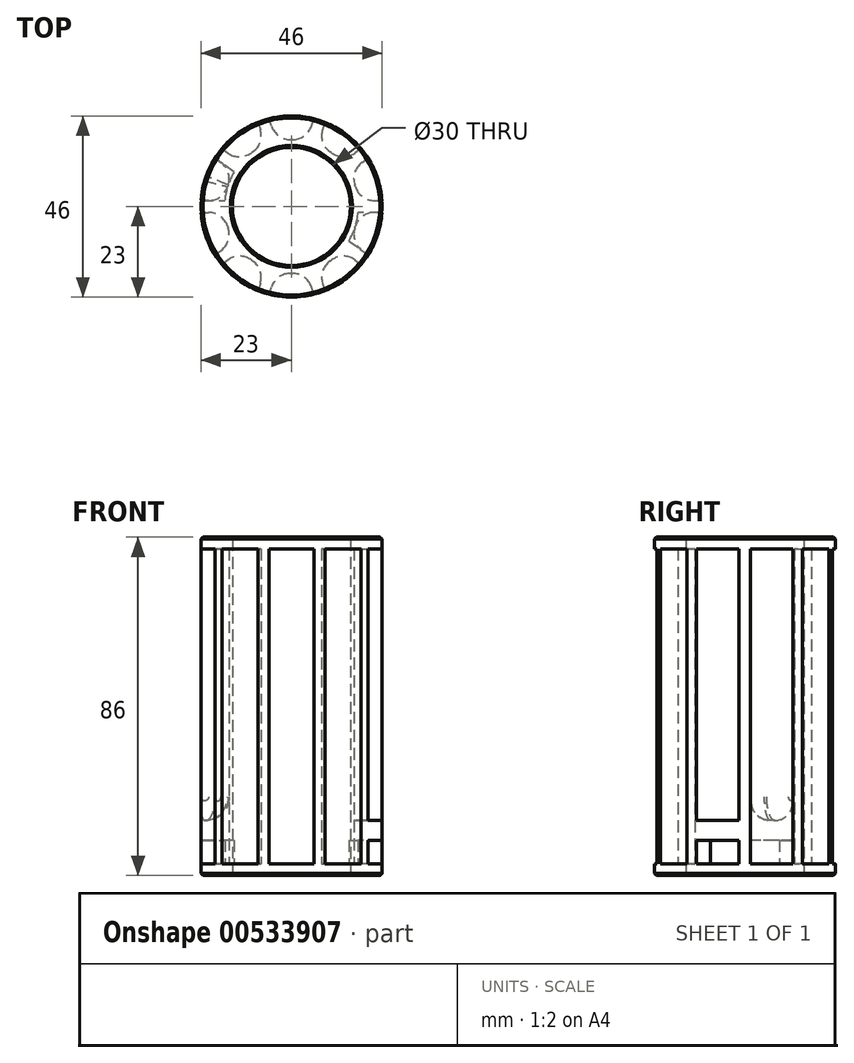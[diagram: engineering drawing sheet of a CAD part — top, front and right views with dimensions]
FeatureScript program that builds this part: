
annotation { "Feature Type Name" : "Feature", "Feature Type Description" : "" }
export const myFeature = defineFeature(function(context is Context, id is Id, definition is map)
    precondition{}
    {
        {
            var Q0;
            Q0=qCreatedBy(makeId("Top.planeOp"),FACE);
            var sketch = newSketch(context, id + "F0", { "sketchPlane" : qUnion([Q0])});
            skCircle(sketch, "E0", {"center": v(0, 0) * mm, "radius": 15 * mm});
            skArc(sketch, "E1", {"start": v(-14.58, 8.74) * mm, "mid": v(-16.17, 5.25) * mm, "end": v(-16.93, 1.5) * mm});
            skLineSegment(sketch, "E2.bottom", {"start": v(22.95, -1.5) * mm, "end": v(16.93, -1.5) * mm});
            skLineSegment(sketch, "E2.top", {"start": v(22.95, 1.5) * mm, "end": v(16.93, 1.5) * mm});
            skLineSegment(sketch, "E3.trimOffspring", {"start": v(-16.93, 1.5) * mm, "end": v(-22.95, 1.5) * mm});
            skLineSegment(sketch, "E4.trimOffspring", {"start": v(-16.93, -1.5) * mm, "end": v(-22.95, -1.5) * mm});
            skPoint(sketch, "E5.orphan", {"position": v(-19.5, -1.5) * mm});
            skPoint(sketch, "E6.orphan", {"position": v(-19.5, 1.5) * mm});
            skPoint(sketch, "E7.orphan", {"position": v(19.5, 1.5) * mm});
            skPoint(sketch, "E2.left.start.orphan", {"position": v(19.5, -1.5) * mm});
            skLineSegment(sketch, "E8.1.0", {"start": v(-6.66, -15.64) * mm, "end": v(-8.52, -21.36) * mm});
            skLineSegment(sketch, "E8.1.1", {"start": v(-3.8, -16.57) * mm, "end": v(-5.67, -22.3) * mm});
            skLineSegment(sketch, "E8.1.2", {"start": v(8.52, 21.36) * mm, "end": v(6.66, 15.64) * mm});
            skLineSegment(sketch, "E8.1.3", {"start": v(5.67, 22.3) * mm, "end": v(3.8, 16.57) * mm});
            skLineSegment(sketch, "E8.2.0", {"start": v(12.82, -11.17) * mm, "end": v(17.69, -14.7) * mm});
            skLineSegment(sketch, "E8.2.1", {"start": v(14.58, -8.74) * mm, "end": v(19.45, -12.28) * mm});
            skLineSegment(sketch, "E8.2.2", {"start": v(-17.69, 14.7) * mm, "end": v(-12.82, 11.17) * mm});
            skLineSegment(sketch, "E8.2.3", {"start": v(-19.45, 12.28) * mm, "end": v(-14.58, 8.74) * mm});
            skLineSegment(sketch, "E8.3.0", {"start": v(14.58, 8.74) * mm, "end": v(19.45, 12.28) * mm});
            skLineSegment(sketch, "E8.3.1", {"start": v(12.82, 11.17) * mm, "end": v(17.69, 14.7) * mm});
            skLineSegment(sketch, "E8.3.2", {"start": v(-19.45, -12.28) * mm, "end": v(-14.58, -8.74) * mm});
            skLineSegment(sketch, "E8.3.3", {"start": v(-17.69, -14.7) * mm, "end": v(-12.82, -11.17) * mm});
            skLineSegment(sketch, "E8.4.0", {"start": v(-3.8, 16.57) * mm, "end": v(-5.67, 22.3) * mm});
            skLineSegment(sketch, "E8.4.1", {"start": v(-6.66, 15.64) * mm, "end": v(-8.52, 21.36) * mm});
            skLineSegment(sketch, "E8.4.2", {"start": v(5.67, -22.3) * mm, "end": v(3.8, -16.57) * mm});
            skLineSegment(sketch, "E8.4.3", {"start": v(8.52, -21.36) * mm, "end": v(6.66, -15.64) * mm});
            skPoint(sketch, "E9.orphan", {"position": v(-16.93, 1.5) * mm});
            skPoint(sketch, "E10.orphan", {"position": v(-16.93, -1.5) * mm});
            skPoint(sketch, "E11.orphan", {"position": v(-14.58, -8.74) * mm});
            skPoint(sketch, "E12.orphan", {"position": v(-12.82, -11.17) * mm});
            skPoint(sketch, "E13.orphan", {"position": v(-14.58, 8.74) * mm});
            skPoint(sketch, "E14.orphan", {"position": v(-12.82, 11.17) * mm});
            skPoint(sketch, "E15.orphan", {"position": v(-6.66, 15.64) * mm});
            skPoint(sketch, "E16.orphan", {"position": v(-3.8, 16.57) * mm});
            skPoint(sketch, "E17.orphan", {"position": v(3.8, 16.57) * mm});
            skPoint(sketch, "E18.orphan", {"position": v(6.66, 15.64) * mm});
            skPoint(sketch, "E19.orphan", {"position": v(12.82, 11.17) * mm});
            skPoint(sketch, "E20.orphan", {"position": v(14.58, 8.74) * mm});
            skPoint(sketch, "E21.orphan", {"position": v(16.93, 1.5) * mm});
            skPoint(sketch, "E22.orphan", {"position": v(16.93, -1.5) * mm});
            skPoint(sketch, "E23.orphan", {"position": v(14.58, -8.74) * mm});
            skPoint(sketch, "E24.orphan", {"position": v(12.82, -11.17) * mm});
            skPoint(sketch, "E25.orphan", {"position": v(6.66, -15.64) * mm});
            skPoint(sketch, "E26.orphan", {"position": v(3.8, -16.57) * mm});
            skPoint(sketch, "E27.orphan", {"position": v(-3.8, -16.57) * mm});
            skPoint(sketch, "E28.orphan", {"position": v(-6.66, -15.64) * mm});
            skCircle(sketch, "E29.0", {"center": v(0, 0) * mm, "radius": 23 * mm});
            skPoint(sketch, "E30.orphan", {"position": v(-12.96, 7.56) * mm});
            skPoint(sketch, "E31.orphan", {"position": v(-11.2, 9.99) * mm});
            skArc(sketch, "E32.trimOffspring", {"start": v(-6.66, 15.64) * mm, "mid": v(-10, 13.75) * mm, "end": v(-12.82, 11.17) * mm});
            skPoint(sketch, "E33.orphan", {"position": v(-3.19, 14.66) * mm});
            skPoint(sketch, "E34.orphan", {"position": v(-6.04, 13.73) * mm});
            skPoint(sketch, "E35.orphan", {"position": v(3.19, 14.66) * mm});
            skArc(sketch, "E36.trimOffspring", {"start": v(3.8, 16.57) * mm, "mid": v(0, 17) * mm, "end": v(-3.8, 16.57) * mm});
            skPoint(sketch, "E37.orphan", {"position": v(6.04, 13.73) * mm});
            skPoint(sketch, "E38.orphan", {"position": v(11.2, 9.99) * mm});
            skArc(sketch, "E39.trimOffspring", {"start": v(12.82, 11.17) * mm, "mid": v(10, 13.75) * mm, "end": v(6.66, 15.64) * mm});
            skPoint(sketch, "E40.orphan", {"position": v(12.96, 7.56) * mm});
            skPoint(sketch, "E41.orphan", {"position": v(14.92, 1.5) * mm});
            skArc(sketch, "E42.trimOffspring", {"start": v(16.93, 1.5) * mm, "mid": v(16.17, 5.25) * mm, "end": v(14.58, 8.74) * mm});
            skPoint(sketch, "E43.orphan", {"position": v(14.92, -1.5) * mm});
            skPoint(sketch, "E44.orphan", {"position": v(12.96, -7.56) * mm});
            skArc(sketch, "E45.trimOffspring", {"start": v(14.58, -8.74) * mm, "mid": v(16.17, -5.25) * mm, "end": v(16.93, -1.5) * mm});
            skPoint(sketch, "E46.orphan", {"position": v(11.2, -9.99) * mm});
            skPoint(sketch, "E47.orphan", {"position": v(6.04, -13.73) * mm});
            skArc(sketch, "E48.trimOffspring", {"start": v(6.66, -15.64) * mm, "mid": v(10, -13.75) * mm, "end": v(12.82, -11.17) * mm});
            skPoint(sketch, "E49.orphan", {"position": v(3.19, -14.66) * mm});
            skPoint(sketch, "E50.orphan", {"position": v(-3.19, -14.66) * mm});
            skArc(sketch, "E51.trimOffspring", {"start": v(-3.8, -16.57) * mm, "mid": v(0, -17) * mm, "end": v(3.8, -16.57) * mm});
            skPoint(sketch, "E52.orphan", {"position": v(-6.04, -13.73) * mm});
            skPoint(sketch, "E53.orphan", {"position": v(-11.2, -9.99) * mm});
            skArc(sketch, "E54.trimOffspring", {"start": v(-12.82, -11.17) * mm, "mid": v(-10, -13.75) * mm, "end": v(-6.66, -15.64) * mm});
            skPoint(sketch, "E55.orphan", {"position": v(-12.96, -7.56) * mm});
            skPoint(sketch, "E56.orphan", {"position": v(-14.92, -1.5) * mm});
            skArc(sketch, "E57.trimOffspring", {"start": v(-16.93, -1.5) * mm, "mid": v(-16.17, -5.25) * mm, "end": v(-14.58, -8.74) * mm});
            skPoint(sketch, "E58.orphan", {"position": v(-14.92, 1.5) * mm});
            skSolve(sketch);
        }
        {
            var Q0;
            Q0=makeQuery(id+"F0.imprint","IMPRINT",FACE,{"disambiguationData":[TD([[makeQuery(id+"F0.imprint","IMPRINT",EDGE,{"derivedFrom":sQuery(id+"F0.wireOp",EDGE,"E0")}),-1.0]])]});
            extrude(context, id + "F1", {"entities" : qUnion([Q0]), "depth" : 86 * mm, "offsetDistance" : 25 * mm});
        }
        {
            var Q0;
            Q0=makeQuery(id+"F1.opExtrude","CAP_FACE",FACE,{"disambiguationData":[OSD([sQuery(id+"F0.wireOp",EDGE,"E0"),sQuery(id+"F0.wireOp",EDGE,"E1"),sQuery(id+"F0.wireOp",EDGE,"E2.bottom"),sQuery(id+"F0.wireOp",EDGE,"E2.top"),sQuery(id+"F0.wireOp",EDGE,"E3.trimOffspring"),sQuery(id+"F0.wireOp",EDGE,"E4.trimOffspring"),sQuery(id+"F0.wireOp",EDGE,"E8.1.0"),sQuery(id+"F0.wireOp",EDGE,"E8.1.1"),sQuery(id+"F0.wireOp",EDGE,"E8.1.2"),sQuery(id+"F0.wireOp",EDGE,"E8.1.3"),sQuery(id+"F0.wireOp",EDGE,"E8.2.0"),sQuery(id+"F0.wireOp",EDGE,"E8.2.1"),sQuery(id+"F0.wireOp",EDGE,"E8.2.2"),sQuery(id+"F0.wireOp",EDGE,"E8.2.3"),sQuery(id+"F0.wireOp",EDGE,"E8.3.0"),sQuery(id+"F0.wireOp",EDGE,"E8.3.1"),sQuery(id+"F0.wireOp",EDGE,"E8.3.2"),sQuery(id+"F0.wireOp",EDGE,"E8.3.3"),sQuery(id+"F0.wireOp",EDGE,"E8.4.0"),sQuery(id+"F0.wireOp",EDGE,"E8.4.1"),sQuery(id+"F0.wireOp",EDGE,"E8.4.2"),sQuery(id+"F0.wireOp",EDGE,"E8.4.3"),sQuery(id+"F0.wireOp",EDGE,"E29.0"),sQuery(id+"F0.wireOp",EDGE,"E32.trimOffspring"),sQuery(id+"F0.wireOp",EDGE,"E36.trimOffspring"),sQuery(id+"F0.wireOp",EDGE,"E39.trimOffspring"),sQuery(id+"F0.wireOp",EDGE,"E42.trimOffspring"),sQuery(id+"F0.wireOp",EDGE,"E45.trimOffspring"),sQuery(id+"F0.wireOp",EDGE,"E48.trimOffspring"),sQuery(id+"F0.wireOp",EDGE,"E51.trimOffspring"),sQuery(id+"F0.wireOp",EDGE,"E54.trimOffspring"),sQuery(id+"F0.wireOp",EDGE,"E57.trimOffspring")])],"isStart":true});
            var sketch = newSketch(context, id + "F2", { "sketchPlane" : qUnion([Q0])});
            skCircle(sketch, "E59", {"center": v(0, 0) * mm, "radius": 23 * mm});
            skCircle(sketch, "E60", {"center": v(0, 0) * mm, "radius": 17 * mm});
            skSolve(sketch);
        }
        {
            var Q0;
            Q0 = qSketchRegion(id + "F2", true);
            extrude(context, id + "F3", {"entities" : qUnion([Q0]), "operationType" : NewBodyOperationType.ADD, "oppositeDirection" : true, "depth" : 3 * mm, "offsetDistance" : 25 * mm});
        }
        {
            var Q0;
            {var subQ1=sQuery(id+"F2.wireOp",EDGE,"E59");var subQ3=sQuery(id+"F0.wireOp",EDGE,"E8.1.3");Q0=makeQuery(id+"F3.boolean.opBoolean","SPLIT",FACE,{"disambiguationData":[TD([makeQuery(id+"F1.opExtrude","SWEPT_FACE",FACE,{"disambiguationData":[OSD([subQ3])]})])],"derivedFrom":makeQuery(id+"F3.opExtrude","CAP_FACE",FACE,{"disambiguationData":[OSD([subQ1,sQuery(id+"F2.wireOp",EDGE,"E60")])],"isStart":false})});}
            var sketch = newSketch(context, id + "F4", { "sketchPlane" : qUnion([Q0])});
            skArc(sketch, "E61.1.0", {"start": v(-16.93, 1.5) * mm, "mid": v(-16.17, 5.25) * mm, "end": v(-14.58, 8.74) * mm});
            skLineSegment(sketch, "E61.1.1", {"start": v(-14.58, 8.74) * mm, "end": v(-19.45, 12.28) * mm});
            skArc(sketch, "E61.1.2", {"start": v(-19.45, 12.28) * mm, "mid": v(-21.87, 7.1) * mm, "end": v(-22.95, 1.5) * mm});
            skLineSegment(sketch, "E61.1.3", {"start": v(-22.95, 1.5) * mm, "end": v(-16.93, 1.5) * mm});
            skLineSegment(sketch, "E62.0.0", {"start": v(14.58, -8.74) * mm, "end": v(19.45, -12.28) * mm});
            skArc(sketch, "E62.0.1", {"start": v(19.45, -12.28) * mm, "mid": v(21.87, -7.1) * mm, "end": v(22.95, -1.5) * mm});
            skLineSegment(sketch, "E62.0.2", {"start": v(22.95, -1.5) * mm, "end": v(16.93, -1.5) * mm});
            skArc(sketch, "E62.0.3", {"start": v(16.93, -1.5) * mm, "mid": v(16.17, -5.25) * mm, "end": v(14.58, -8.74) * mm});
            skSolve(sketch);
        }
        {
            var Q0;
            Q0 = qSketchRegion(id + "F4", true);
            extrude(context, id + "F5", {"entities" : qUnion([Q0]), "depth" : 5 * mm, "offsetDistance" : 25 * mm});
        }
        {
            var Q0;
            Q0=makeQuery(id+"F5.opExtrude","SWEPT_BODY",BODY,{"disambiguationData":[OSD([sQuery(id+"F4.wireOp",EDGE,"E61.1.0"),sQuery(id+"F4.wireOp",EDGE,"E61.1.1"),sQuery(id+"F4.wireOp",EDGE,"E61.1.2"),sQuery(id+"F4.wireOp",EDGE,"E61.1.3")])]});
            var Q1;
            Q1=makeQuery(id+"F5.opExtrude","SWEPT_BODY",BODY,{"disambiguationData":[OSD([sQuery(id+"F4.wireOp",EDGE,"E62.0.0"),sQuery(id+"F4.wireOp",EDGE,"E62.0.1"),sQuery(id+"F4.wireOp",EDGE,"E62.0.2"),sQuery(id+"F4.wireOp",EDGE,"E62.0.3")])]});
            transform(context, id + "F6", {"entities" : qUnion([Q0, Q1]), "transformType" : TransformType.TRANSLATION_3D, "dx" : 0 * mm, "dy" : 0 * mm, "dz" : 6 * mm, "makeCopy" : false});
        }
        {
            var Q0;
            Q0=makeQuery(id+"F5.opExtrude","SWEPT_BODY",BODY,{"disambiguationData":[OSD([sQuery(id+"F4.wireOp",EDGE,"E61.1.0"),sQuery(id+"F4.wireOp",EDGE,"E61.1.1"),sQuery(id+"F4.wireOp",EDGE,"E61.1.2"),sQuery(id+"F4.wireOp",EDGE,"E61.1.3")])]});
            var Q1;
            Q1=makeQuery(id+"F1.opExtrude","SWEPT_BODY",BODY,{"disambiguationData":[OSD([sQuery(id+"F0.wireOp",EDGE,"E0"),sQuery(id+"F0.wireOp",EDGE,"E1"),sQuery(id+"F0.wireOp",EDGE,"E2.bottom"),sQuery(id+"F0.wireOp",EDGE,"E2.top"),sQuery(id+"F0.wireOp",EDGE,"E3.trimOffspring"),sQuery(id+"F0.wireOp",EDGE,"E4.trimOffspring"),sQuery(id+"F0.wireOp",EDGE,"E8.1.0"),sQuery(id+"F0.wireOp",EDGE,"E8.1.1"),sQuery(id+"F0.wireOp",EDGE,"E8.1.2"),sQuery(id+"F0.wireOp",EDGE,"E8.1.3"),sQuery(id+"F0.wireOp",EDGE,"E8.2.0"),sQuery(id+"F0.wireOp",EDGE,"E8.2.1"),sQuery(id+"F0.wireOp",EDGE,"E8.2.2"),sQuery(id+"F0.wireOp",EDGE,"E8.2.3"),sQuery(id+"F0.wireOp",EDGE,"E8.3.0"),sQuery(id+"F0.wireOp",EDGE,"E8.3.1"),sQuery(id+"F0.wireOp",EDGE,"E8.3.2"),sQuery(id+"F0.wireOp",EDGE,"E8.3.3"),sQuery(id+"F0.wireOp",EDGE,"E8.4.0"),sQuery(id+"F0.wireOp",EDGE,"E8.4.1"),sQuery(id+"F0.wireOp",EDGE,"E8.4.2"),sQuery(id+"F0.wireOp",EDGE,"E8.4.3"),sQuery(id+"F0.wireOp",EDGE,"E29.0"),sQuery(id+"F0.wireOp",EDGE,"E32.trimOffspring"),sQuery(id+"F0.wireOp",EDGE,"E36.trimOffspring"),sQuery(id+"F0.wireOp",EDGE,"E39.trimOffspring"),sQuery(id+"F0.wireOp",EDGE,"E42.trimOffspring"),sQuery(id+"F0.wireOp",EDGE,"E45.trimOffspring"),sQuery(id+"F0.wireOp",EDGE,"E48.trimOffspring"),sQuery(id+"F0.wireOp",EDGE,"E51.trimOffspring"),sQuery(id+"F0.wireOp",EDGE,"E54.trimOffspring"),sQuery(id+"F0.wireOp",EDGE,"E57.trimOffspring")])]});
            var Q2;
            Q2=makeQuery(id+"F5.opExtrude","SWEPT_BODY",BODY,{"disambiguationData":[OSD([sQuery(id+"F4.wireOp",EDGE,"E62.0.0"),sQuery(id+"F4.wireOp",EDGE,"E62.0.1"),sQuery(id+"F4.wireOp",EDGE,"E62.0.2"),sQuery(id+"F4.wireOp",EDGE,"E62.0.3")])]});
            booleanBodies(context, id + "F7", {"operationType" : BooleanOperationType.UNION, "tools" : qUnion([Q0, Q1, Q2])});
        }
        {
            var Q0;
            Q0=makeQuery(id+"F1.opExtrude","CAP_FACE",FACE,{"disambiguationData":[OSD([sQuery(id+"F0.wireOp",EDGE,"E0"),sQuery(id+"F0.wireOp",EDGE,"E1"),sQuery(id+"F0.wireOp",EDGE,"E2.bottom"),sQuery(id+"F0.wireOp",EDGE,"E2.top"),sQuery(id+"F0.wireOp",EDGE,"E3.trimOffspring"),sQuery(id+"F0.wireOp",EDGE,"E4.trimOffspring"),sQuery(id+"F0.wireOp",EDGE,"E8.1.0"),sQuery(id+"F0.wireOp",EDGE,"E8.1.1"),sQuery(id+"F0.wireOp",EDGE,"E8.1.2"),sQuery(id+"F0.wireOp",EDGE,"E8.1.3"),sQuery(id+"F0.wireOp",EDGE,"E8.2.0"),sQuery(id+"F0.wireOp",EDGE,"E8.2.1"),sQuery(id+"F0.wireOp",EDGE,"E8.2.2"),sQuery(id+"F0.wireOp",EDGE,"E8.2.3"),sQuery(id+"F0.wireOp",EDGE,"E8.3.0"),sQuery(id+"F0.wireOp",EDGE,"E8.3.1"),sQuery(id+"F0.wireOp",EDGE,"E8.3.2"),sQuery(id+"F0.wireOp",EDGE,"E8.3.3"),sQuery(id+"F0.wireOp",EDGE,"E8.4.0"),sQuery(id+"F0.wireOp",EDGE,"E8.4.1"),sQuery(id+"F0.wireOp",EDGE,"E8.4.2"),sQuery(id+"F0.wireOp",EDGE,"E8.4.3"),sQuery(id+"F0.wireOp",EDGE,"E29.0"),sQuery(id+"F0.wireOp",EDGE,"E32.trimOffspring"),sQuery(id+"F0.wireOp",EDGE,"E36.trimOffspring"),sQuery(id+"F0.wireOp",EDGE,"E39.trimOffspring"),sQuery(id+"F0.wireOp",EDGE,"E42.trimOffspring"),sQuery(id+"F0.wireOp",EDGE,"E45.trimOffspring"),sQuery(id+"F0.wireOp",EDGE,"E48.trimOffspring"),sQuery(id+"F0.wireOp",EDGE,"E51.trimOffspring"),sQuery(id+"F0.wireOp",EDGE,"E54.trimOffspring"),sQuery(id+"F0.wireOp",EDGE,"E57.trimOffspring")])],"isStart":false});
            var sketch = newSketch(context, id + "F8", { "sketchPlane" : qUnion([Q0])});
            skPoint(sketch, "E63.first.point", {"position": v(22.95, -1.5) * mm});
            skPoint(sketch, "E63.second.point", {"position": v(-8.52, 21.36) * mm});
            skPoint(sketch, "E63.third.point", {"position": v(-19.45, -12.28) * mm});
            skCircle(sketch, "E64", {"center": v(0, 0) * mm, "radius": 23 * mm});
            skCircle(sketch, "E65", {"center": v(0, 0) * mm, "radius": 17 * mm});
            skSolve(sketch);
        }
        {
            var Q0;
            Q0 = qSketchRegion(id + "F8", true);
            extrude(context, id + "F9", {"entities" : qUnion([Q0]), "operationType" : NewBodyOperationType.ADD, "oppositeDirection" : true, "depth" : 3 * mm, "offsetDistance" : 25 * mm});
        }
        {
            var Q0;
            {var subQ0=sQuery(id+"F8.wireOp",EDGE,"E65");Q0=makeQuery(id+"F9.boolean.opBoolean","SPLIT",EDGE,{"disambiguationData":[topologyDisambiguationEdgeConnected([makeQuery(id+"F1.opExtrude","SWEPT_FACE",FACE,{"disambiguationData":[OSD([sQuery(id+"F0.wireOp",EDGE,"E57.trimOffspring")])]})])],"derivedFrom":makeQuery(id+"F9.opExtrude","CAP_EDGE",EDGE,{"disambiguationData":[OSD([subQ0])],"isStart":false})});}
            var Q1;
            {var subQ0=sQuery(id+"F8.wireOp",EDGE,"E65");Q1=makeQuery(id+"F9.boolean.opBoolean","SPLIT",EDGE,{"disambiguationData":[topologyDisambiguationEdgeConnected([makeQuery(id+"F1.opExtrude","SWEPT_FACE",FACE,{"disambiguationData":[OSD([sQuery(id+"F0.wireOp",EDGE,"E54.trimOffspring")])]})])],"derivedFrom":makeQuery(id+"F9.opExtrude","CAP_EDGE",EDGE,{"disambiguationData":[OSD([subQ0])],"isStart":false})});}
            var Q2;
            {var subQ0=sQuery(id+"F8.wireOp",EDGE,"E65");Q2=makeQuery(id+"F9.boolean.opBoolean","SPLIT",EDGE,{"disambiguationData":[topologyDisambiguationEdgeConnected([makeQuery(id+"F1.opExtrude","SWEPT_FACE",FACE,{"disambiguationData":[OSD([sQuery(id+"F0.wireOp",EDGE,"E1")])]})])],"derivedFrom":makeQuery(id+"F9.opExtrude","CAP_EDGE",EDGE,{"disambiguationData":[OSD([subQ0])],"isStart":false})});}
            var Q3;
            {var subQ0=sQuery(id+"F8.wireOp",EDGE,"E65");Q3=makeQuery(id+"F9.boolean.opBoolean","SPLIT",EDGE,{"disambiguationData":[topologyDisambiguationEdgeConnected([makeQuery(id+"F1.opExtrude","SWEPT_FACE",FACE,{"disambiguationData":[OSD([sQuery(id+"F0.wireOp",EDGE,"E32.trimOffspring")])]})])],"derivedFrom":makeQuery(id+"F9.opExtrude","CAP_EDGE",EDGE,{"disambiguationData":[OSD([subQ0])],"isStart":false})});}
            var Q4;
            {var subQ0=sQuery(id+"F8.wireOp",EDGE,"E65");Q4=makeQuery(id+"F9.boolean.opBoolean","SPLIT",EDGE,{"disambiguationData":[topologyDisambiguationEdgeConnected([makeQuery(id+"F1.opExtrude","SWEPT_FACE",FACE,{"disambiguationData":[OSD([sQuery(id+"F0.wireOp",EDGE,"E36.trimOffspring")])]})])],"derivedFrom":makeQuery(id+"F9.opExtrude","CAP_EDGE",EDGE,{"disambiguationData":[OSD([subQ0])],"isStart":false})});}
            var Q5;
            {var subQ0=sQuery(id+"F8.wireOp",EDGE,"E65");Q5=makeQuery(id+"F9.boolean.opBoolean","SPLIT",EDGE,{"disambiguationData":[topologyDisambiguationEdgeConnected([makeQuery(id+"F1.opExtrude","SWEPT_FACE",FACE,{"disambiguationData":[OSD([sQuery(id+"F0.wireOp",EDGE,"E39.trimOffspring")])]})])],"derivedFrom":makeQuery(id+"F9.opExtrude","CAP_EDGE",EDGE,{"disambiguationData":[OSD([subQ0])],"isStart":false})});}
            var Q6;
            {var subQ0=sQuery(id+"F8.wireOp",EDGE,"E65");Q6=makeQuery(id+"F9.boolean.opBoolean","SPLIT",EDGE,{"disambiguationData":[topologyDisambiguationEdgeConnected([makeQuery(id+"F1.opExtrude","SWEPT_FACE",FACE,{"disambiguationData":[OSD([sQuery(id+"F0.wireOp",EDGE,"E42.trimOffspring")])]})])],"derivedFrom":makeQuery(id+"F9.opExtrude","CAP_EDGE",EDGE,{"disambiguationData":[OSD([subQ0])],"isStart":false})});}
            var Q7;
            {var subQ0=sQuery(id+"F8.wireOp",EDGE,"E65");Q7=makeQuery(id+"F9.boolean.opBoolean","SPLIT",EDGE,{"disambiguationData":[topologyDisambiguationEdgeConnected([makeQuery(id+"F1.opExtrude","SWEPT_FACE",FACE,{"disambiguationData":[OSD([sQuery(id+"F0.wireOp",EDGE,"E45.trimOffspring")])]})])],"derivedFrom":makeQuery(id+"F9.opExtrude","CAP_EDGE",EDGE,{"disambiguationData":[OSD([subQ0])],"isStart":false})});}
            var Q8;
            {var subQ0=sQuery(id+"F8.wireOp",EDGE,"E65");Q8=makeQuery(id+"F9.boolean.opBoolean","SPLIT",EDGE,{"disambiguationData":[topologyDisambiguationEdgeConnected([makeQuery(id+"F1.opExtrude","SWEPT_FACE",FACE,{"disambiguationData":[OSD([sQuery(id+"F0.wireOp",EDGE,"E48.trimOffspring")])]})])],"derivedFrom":makeQuery(id+"F9.opExtrude","CAP_EDGE",EDGE,{"disambiguationData":[OSD([subQ0])],"isStart":false})});}
            var Q9;
            {var subQ0=sQuery(id+"F8.wireOp",EDGE,"E65");Q9=makeQuery(id+"F9.boolean.opBoolean","SPLIT",EDGE,{"disambiguationData":[topologyDisambiguationEdgeConnected([makeQuery(id+"F1.opExtrude","SWEPT_FACE",FACE,{"disambiguationData":[OSD([sQuery(id+"F0.wireOp",EDGE,"E51.trimOffspring")])]})])],"derivedFrom":makeQuery(id+"F9.opExtrude","CAP_EDGE",EDGE,{"disambiguationData":[OSD([subQ0])],"isStart":false})});}
            var Q10;
            {var subQ0=sQuery(id+"F2.wireOp",EDGE,"E60");Q10=makeQuery(id+"F3.boolean.opBoolean","SPLIT",EDGE,{"disambiguationData":[topologyDisambiguationEdgeConnected([makeQuery(id+"F1.opExtrude","SWEPT_FACE",FACE,{"disambiguationData":[OSD([sQuery(id+"F0.wireOp",EDGE,"E42.trimOffspring")])]})])],"derivedFrom":makeQuery(id+"F3.opExtrude","CAP_EDGE",EDGE,{"disambiguationData":[OSD([subQ0])],"isStart":false})});}
            var Q11;
            {var subQ0=sQuery(id+"F2.wireOp",EDGE,"E60");Q11=makeQuery(id+"F3.boolean.opBoolean","SPLIT",EDGE,{"disambiguationData":[topologyDisambiguationEdgeConnected([makeQuery(id+"F1.opExtrude","SWEPT_FACE",FACE,{"disambiguationData":[OSD([sQuery(id+"F0.wireOp",EDGE,"E39.trimOffspring")])]})])],"derivedFrom":makeQuery(id+"F3.opExtrude","CAP_EDGE",EDGE,{"disambiguationData":[OSD([subQ0])],"isStart":false})});}
            var Q12;
            {var subQ0=sQuery(id+"F2.wireOp",EDGE,"E60");Q12=makeQuery(id+"F3.boolean.opBoolean","SPLIT",EDGE,{"disambiguationData":[topologyDisambiguationEdgeConnected([makeQuery(id+"F1.opExtrude","SWEPT_FACE",FACE,{"disambiguationData":[OSD([sQuery(id+"F0.wireOp",EDGE,"E36.trimOffspring")])]})])],"derivedFrom":makeQuery(id+"F3.opExtrude","CAP_EDGE",EDGE,{"disambiguationData":[OSD([subQ0])],"isStart":false})});}
            var Q13;
            {var subQ0=sQuery(id+"F2.wireOp",EDGE,"E60");Q13=makeQuery(id+"F3.boolean.opBoolean","SPLIT",EDGE,{"disambiguationData":[topologyDisambiguationEdgeConnected([makeQuery(id+"F1.opExtrude","SWEPT_FACE",FACE,{"disambiguationData":[OSD([sQuery(id+"F0.wireOp",EDGE,"E32.trimOffspring")])]})])],"derivedFrom":makeQuery(id+"F3.opExtrude","CAP_EDGE",EDGE,{"disambiguationData":[OSD([subQ0])],"isStart":false})});}
            var Q14;
            Q14=makeQuery(id+"F5.opExtrude","CAP_EDGE",EDGE,{"disambiguationData":[OSD([sQuery(id+"F4.wireOp",EDGE,"E61.1.0")])],"isStart":false});
            var Q15;
            {var subQ0=sQuery(id+"F2.wireOp",EDGE,"E60");Q15=makeQuery(id+"F3.boolean.opBoolean","SPLIT",EDGE,{"disambiguationData":[topologyDisambiguationEdgeConnected([makeQuery(id+"F1.opExtrude","SWEPT_FACE",FACE,{"disambiguationData":[OSD([sQuery(id+"F0.wireOp",EDGE,"E57.trimOffspring")])]})])],"derivedFrom":makeQuery(id+"F3.opExtrude","CAP_EDGE",EDGE,{"disambiguationData":[OSD([subQ0])],"isStart":false})});}
            var Q16;
            {var subQ0=sQuery(id+"F2.wireOp",EDGE,"E60");Q16=makeQuery(id+"F3.boolean.opBoolean","SPLIT",EDGE,{"disambiguationData":[topologyDisambiguationEdgeConnected([makeQuery(id+"F1.opExtrude","SWEPT_FACE",FACE,{"disambiguationData":[OSD([sQuery(id+"F0.wireOp",EDGE,"E54.trimOffspring")])]})])],"derivedFrom":makeQuery(id+"F3.opExtrude","CAP_EDGE",EDGE,{"disambiguationData":[OSD([subQ0])],"isStart":false})});}
            var Q17;
            {var subQ0=sQuery(id+"F2.wireOp",EDGE,"E60");Q17=makeQuery(id+"F3.boolean.opBoolean","SPLIT",EDGE,{"disambiguationData":[topologyDisambiguationEdgeConnected([makeQuery(id+"F1.opExtrude","SWEPT_FACE",FACE,{"disambiguationData":[OSD([sQuery(id+"F0.wireOp",EDGE,"E51.trimOffspring")])]})])],"derivedFrom":makeQuery(id+"F3.opExtrude","CAP_EDGE",EDGE,{"disambiguationData":[OSD([subQ0])],"isStart":false})});}
            var Q18;
            {var subQ0=sQuery(id+"F2.wireOp",EDGE,"E60");Q18=makeQuery(id+"F3.boolean.opBoolean","SPLIT",EDGE,{"disambiguationData":[topologyDisambiguationEdgeConnected([makeQuery(id+"F1.opExtrude","SWEPT_FACE",FACE,{"disambiguationData":[OSD([sQuery(id+"F0.wireOp",EDGE,"E48.trimOffspring")])]})])],"derivedFrom":makeQuery(id+"F3.opExtrude","CAP_EDGE",EDGE,{"disambiguationData":[OSD([subQ0])],"isStart":false})});}
            var Q19;
            Q19=makeQuery(id+"F5.opExtrude","CAP_EDGE",EDGE,{"disambiguationData":[OSD([sQuery(id+"F4.wireOp",EDGE,"E62.0.3")])],"isStart":false});
            fillet(context, id + "F10", {"entities" : qUnion([Q0, Q1, Q2, Q3, Q4, Q5, Q6, Q7, Q8, Q9, Q10, Q11, Q12, Q13, Q14, Q15, Q16, Q17, Q18, Q19]), "radius" : 6 * mm, "tangentPropagation" : true, "allowEdgeOverflow" : false});
        }
        {
            var Q0;
            Q0=makeQuery(id+"F1.opExtrude","SWEPT_EDGE",EDGE,{"disambiguationData":[OSD([sQuery(id+"F0.wireOp",EDGE,"E4.trimOffspring"),sQuery(id+"F0.wireOp",EDGE,"E57.trimOffspring")])]});
            var Q1;
            Q1=makeQuery(id+"F1.opExtrude","SWEPT_EDGE",EDGE,{"disambiguationData":[OSD([sQuery(id+"F0.wireOp",EDGE,"E8.3.2"),sQuery(id+"F0.wireOp",EDGE,"E57.trimOffspring")])]});
            var Q2;
            Q2=makeQuery(id+"F1.opExtrude","SWEPT_EDGE",EDGE,{"disambiguationData":[OSD([sQuery(id+"F0.wireOp",EDGE,"E8.3.3"),sQuery(id+"F0.wireOp",EDGE,"E54.trimOffspring")])]});
            var Q3;
            Q3=makeQuery(id+"F1.opExtrude","SWEPT_EDGE",EDGE,{"disambiguationData":[OSD([sQuery(id+"F0.wireOp",EDGE,"E8.1.0"),sQuery(id+"F0.wireOp",EDGE,"E54.trimOffspring")])]});
            var Q4;
            Q4=makeQuery(id+"F1.opExtrude","SWEPT_EDGE",EDGE,{"disambiguationData":[OSD([sQuery(id+"F0.wireOp",EDGE,"E8.4.2"),sQuery(id+"F0.wireOp",EDGE,"E51.trimOffspring")])]});
            var Q5;
            Q5=makeQuery(id+"F1.opExtrude","SWEPT_EDGE",EDGE,{"disambiguationData":[OSD([sQuery(id+"F0.wireOp",EDGE,"E8.1.1"),sQuery(id+"F0.wireOp",EDGE,"E51.trimOffspring")])]});
            var Q6;
            Q6=makeQuery(id+"F1.opExtrude","SWEPT_EDGE",EDGE,{"disambiguationData":[OSD([sQuery(id+"F0.wireOp",EDGE,"E8.2.0"),sQuery(id+"F0.wireOp",EDGE,"E48.trimOffspring")])]});
            var Q7;
            Q7=makeQuery(id+"F1.opExtrude","SWEPT_EDGE",EDGE,{"disambiguationData":[OSD([sQuery(id+"F0.wireOp",EDGE,"E8.4.3"),sQuery(id+"F0.wireOp",EDGE,"E48.trimOffspring")])]});
            var Q8;
            {var subQ0=sQuery(id+"F0.wireOp",EDGE,"E45.trimOffspring");var subQ1=sQuery(id+"F0.wireOp",EDGE,"E2.bottom");Q8=makeQuery(id+"F7.opBoolean","SPLIT",EDGE,{"disambiguationData":[TD([makeQuery(id+"F5.opExtrude","CAP_FACE",FACE,{"disambiguationData":[OSD([sQuery(id+"F4.wireOp",EDGE,"E62.0.0"),sQuery(id+"F4.wireOp",EDGE,"E62.0.1"),sQuery(id+"F4.wireOp",EDGE,"E62.0.2"),sQuery(id+"F4.wireOp",EDGE,"E62.0.3")])],"isStart":false})])],"derivedFrom":makeQuery(id+"F1.opExtrude","SWEPT_EDGE",EDGE,{"disambiguationData":[OSD([subQ1,subQ0])]})});}
            var Q9;
            {var subQ0=sQuery(id+"F0.wireOp",EDGE,"E45.trimOffspring");var subQ1=sQuery(id+"F0.wireOp",EDGE,"E8.2.1");Q9=makeQuery(id+"F7.opBoolean","SPLIT",EDGE,{"disambiguationData":[TD([makeQuery(id+"F5.opExtrude","CAP_FACE",FACE,{"disambiguationData":[OSD([sQuery(id+"F4.wireOp",EDGE,"E62.0.0"),sQuery(id+"F4.wireOp",EDGE,"E62.0.1"),sQuery(id+"F4.wireOp",EDGE,"E62.0.2"),sQuery(id+"F4.wireOp",EDGE,"E62.0.3")])],"isStart":false})])],"derivedFrom":makeQuery(id+"F1.opExtrude","SWEPT_EDGE",EDGE,{"disambiguationData":[OSD([subQ1,subQ0])]})});}
            var Q10;
            Q10=makeQuery(id+"F1.opExtrude","SWEPT_EDGE",EDGE,{"disambiguationData":[OSD([sQuery(id+"F0.wireOp",EDGE,"E8.3.0"),sQuery(id+"F0.wireOp",EDGE,"E42.trimOffspring")])]});
            var Q11;
            Q11=makeQuery(id+"F1.opExtrude","SWEPT_EDGE",EDGE,{"disambiguationData":[OSD([sQuery(id+"F0.wireOp",EDGE,"E2.top"),sQuery(id+"F0.wireOp",EDGE,"E42.trimOffspring")])]});
            var Q12;
            Q12=makeQuery(id+"F1.opExtrude","SWEPT_EDGE",EDGE,{"disambiguationData":[OSD([sQuery(id+"F0.wireOp",EDGE,"E8.1.2"),sQuery(id+"F0.wireOp",EDGE,"E39.trimOffspring")])]});
            var Q13;
            Q13=makeQuery(id+"F1.opExtrude","SWEPT_EDGE",EDGE,{"disambiguationData":[OSD([sQuery(id+"F0.wireOp",EDGE,"E8.3.1"),sQuery(id+"F0.wireOp",EDGE,"E39.trimOffspring")])]});
            var Q14;
            Q14=makeQuery(id+"F1.opExtrude","SWEPT_EDGE",EDGE,{"disambiguationData":[OSD([sQuery(id+"F0.wireOp",EDGE,"E8.4.0"),sQuery(id+"F0.wireOp",EDGE,"E36.trimOffspring")])]});
            var Q15;
            Q15=makeQuery(id+"F1.opExtrude","SWEPT_EDGE",EDGE,{"disambiguationData":[OSD([sQuery(id+"F0.wireOp",EDGE,"E8.2.2"),sQuery(id+"F0.wireOp",EDGE,"E32.trimOffspring")])]});
            var Q16;
            Q16=makeQuery(id+"F1.opExtrude","SWEPT_EDGE",EDGE,{"disambiguationData":[OSD([sQuery(id+"F0.wireOp",EDGE,"E8.4.1"),sQuery(id+"F0.wireOp",EDGE,"E32.trimOffspring")])]});
            var Q17;
            Q17=makeQuery(id+"F1.opExtrude","SWEPT_EDGE",EDGE,{"disambiguationData":[OSD([sQuery(id+"F0.wireOp",EDGE,"E8.1.3"),sQuery(id+"F0.wireOp",EDGE,"E36.trimOffspring")])]});
            var Q18;
            {var subQ0=sQuery(id+"F0.wireOp",EDGE,"E8.2.3");var subQ1=sQuery(id+"F0.wireOp",EDGE,"E1");Q18=makeQuery(id+"F7.opBoolean","SPLIT",EDGE,{"disambiguationData":[TD([makeQuery(id+"F5.opExtrude","CAP_FACE",FACE,{"disambiguationData":[OSD([sQuery(id+"F4.wireOp",EDGE,"E61.1.0"),sQuery(id+"F4.wireOp",EDGE,"E61.1.1"),sQuery(id+"F4.wireOp",EDGE,"E61.1.2"),sQuery(id+"F4.wireOp",EDGE,"E61.1.3")])],"isStart":false})])],"derivedFrom":makeQuery(id+"F1.opExtrude","SWEPT_EDGE",EDGE,{"disambiguationData":[OSD([subQ1,subQ0])]})});}
            var Q19;
            {var subQ0=sQuery(id+"F0.wireOp",EDGE,"E3.trimOffspring");var subQ1=sQuery(id+"F0.wireOp",EDGE,"E1");Q19=makeQuery(id+"F7.opBoolean","SPLIT",EDGE,{"disambiguationData":[TD([makeQuery(id+"F5.opExtrude","CAP_FACE",FACE,{"disambiguationData":[OSD([sQuery(id+"F4.wireOp",EDGE,"E61.1.0"),sQuery(id+"F4.wireOp",EDGE,"E61.1.1"),sQuery(id+"F4.wireOp",EDGE,"E61.1.2"),sQuery(id+"F4.wireOp",EDGE,"E61.1.3")])],"isStart":false})])],"derivedFrom":makeQuery(id+"F1.opExtrude","SWEPT_EDGE",EDGE,{"disambiguationData":[OSD([subQ1,subQ0])]})});}
            fillet(context, id + "F11", {"entities" : qUnion([Q0, Q1, Q2, Q3, Q4, Q5, Q6, Q7, Q8, Q9, Q10, Q11, Q12, Q13, Q14, Q15, Q16, Q17, Q18, Q19]), "radius" : 5 * mm, "tangentPropagation" : true, "allowEdgeOverflow" : false});
        }
        {
            var Q0;
            Q0=makeQuery(id+"F9.boolean.opBoolean","MERGE",FACE,{"derivedFrom":[makeQuery(id+"F1.opExtrude","CAP_FACE",FACE,{"disambiguationData":[OSD([sQuery(id+"F0.wireOp",EDGE,"E0"),sQuery(id+"F0.wireOp",EDGE,"E1"),sQuery(id+"F0.wireOp",EDGE,"E2.bottom"),sQuery(id+"F0.wireOp",EDGE,"E2.top"),sQuery(id+"F0.wireOp",EDGE,"E3.trimOffspring"),sQuery(id+"F0.wireOp",EDGE,"E4.trimOffspring"),sQuery(id+"F0.wireOp",EDGE,"E8.1.0"),sQuery(id+"F0.wireOp",EDGE,"E8.1.1"),sQuery(id+"F0.wireOp",EDGE,"E8.1.2"),sQuery(id+"F0.wireOp",EDGE,"E8.1.3"),sQuery(id+"F0.wireOp",EDGE,"E8.2.0"),sQuery(id+"F0.wireOp",EDGE,"E8.2.1"),sQuery(id+"F0.wireOp",EDGE,"E8.2.2"),sQuery(id+"F0.wireOp",EDGE,"E8.2.3"),sQuery(id+"F0.wireOp",EDGE,"E8.3.0"),sQuery(id+"F0.wireOp",EDGE,"E8.3.1"),sQuery(id+"F0.wireOp",EDGE,"E8.3.2"),sQuery(id+"F0.wireOp",EDGE,"E8.3.3"),sQuery(id+"F0.wireOp",EDGE,"E8.4.0"),sQuery(id+"F0.wireOp",EDGE,"E8.4.1"),sQuery(id+"F0.wireOp",EDGE,"E8.4.2"),sQuery(id+"F0.wireOp",EDGE,"E8.4.3"),sQuery(id+"F0.wireOp",EDGE,"E29.0"),sQuery(id+"F0.wireOp",EDGE,"E32.trimOffspring"),sQuery(id+"F0.wireOp",EDGE,"E36.trimOffspring"),sQuery(id+"F0.wireOp",EDGE,"E39.trimOffspring"),sQuery(id+"F0.wireOp",EDGE,"E42.trimOffspring"),sQuery(id+"F0.wireOp",EDGE,"E45.trimOffspring"),sQuery(id+"F0.wireOp",EDGE,"E48.trimOffspring"),sQuery(id+"F0.wireOp",EDGE,"E51.trimOffspring"),sQuery(id+"F0.wireOp",EDGE,"E54.trimOffspring"),sQuery(id+"F0.wireOp",EDGE,"E57.trimOffspring")])],"isStart":false}),makeQuery(id+"F9.opExtrude","CAP_FACE",FACE,{"disambiguationData":[OSD([sQuery(id+"F8.wireOp",EDGE,"E64"),sQuery(id+"F8.wireOp",EDGE,"E65")])],"isStart":true})]});
            var Q1;
            Q1=makeQuery(id+"F3.boolean.opBoolean","MERGE",FACE,{"derivedFrom":[makeQuery(id+"F1.opExtrude","CAP_FACE",FACE,{"disambiguationData":[OSD([sQuery(id+"F0.wireOp",EDGE,"E0"),sQuery(id+"F0.wireOp",EDGE,"E1"),sQuery(id+"F0.wireOp",EDGE,"E2.bottom"),sQuery(id+"F0.wireOp",EDGE,"E2.top"),sQuery(id+"F0.wireOp",EDGE,"E3.trimOffspring"),sQuery(id+"F0.wireOp",EDGE,"E4.trimOffspring"),sQuery(id+"F0.wireOp",EDGE,"E8.1.0"),sQuery(id+"F0.wireOp",EDGE,"E8.1.1"),sQuery(id+"F0.wireOp",EDGE,"E8.1.2"),sQuery(id+"F0.wireOp",EDGE,"E8.1.3"),sQuery(id+"F0.wireOp",EDGE,"E8.2.0"),sQuery(id+"F0.wireOp",EDGE,"E8.2.1"),sQuery(id+"F0.wireOp",EDGE,"E8.2.2"),sQuery(id+"F0.wireOp",EDGE,"E8.2.3"),sQuery(id+"F0.wireOp",EDGE,"E8.3.0"),sQuery(id+"F0.wireOp",EDGE,"E8.3.1"),sQuery(id+"F0.wireOp",EDGE,"E8.3.2"),sQuery(id+"F0.wireOp",EDGE,"E8.3.3"),sQuery(id+"F0.wireOp",EDGE,"E8.4.0"),sQuery(id+"F0.wireOp",EDGE,"E8.4.1"),sQuery(id+"F0.wireOp",EDGE,"E8.4.2"),sQuery(id+"F0.wireOp",EDGE,"E8.4.3"),sQuery(id+"F0.wireOp",EDGE,"E29.0"),sQuery(id+"F0.wireOp",EDGE,"E32.trimOffspring"),sQuery(id+"F0.wireOp",EDGE,"E36.trimOffspring"),sQuery(id+"F0.wireOp",EDGE,"E39.trimOffspring"),sQuery(id+"F0.wireOp",EDGE,"E42.trimOffspring"),sQuery(id+"F0.wireOp",EDGE,"E45.trimOffspring"),sQuery(id+"F0.wireOp",EDGE,"E48.trimOffspring"),sQuery(id+"F0.wireOp",EDGE,"E51.trimOffspring"),sQuery(id+"F0.wireOp",EDGE,"E54.trimOffspring"),sQuery(id+"F0.wireOp",EDGE,"E57.trimOffspring")])],"isStart":true}),makeQuery(id+"F3.opExtrude","CAP_FACE",FACE,{"disambiguationData":[OSD([sQuery(id+"F2.wireOp",EDGE,"E59"),sQuery(id+"F2.wireOp",EDGE,"E60")])],"isStart":true})]});
            chamfer(context, id + "F12", {"entities" : qUnion([Q0, Q1]), "width" : .5 * mm, "tangentPropagation" : true});
        }
    });
